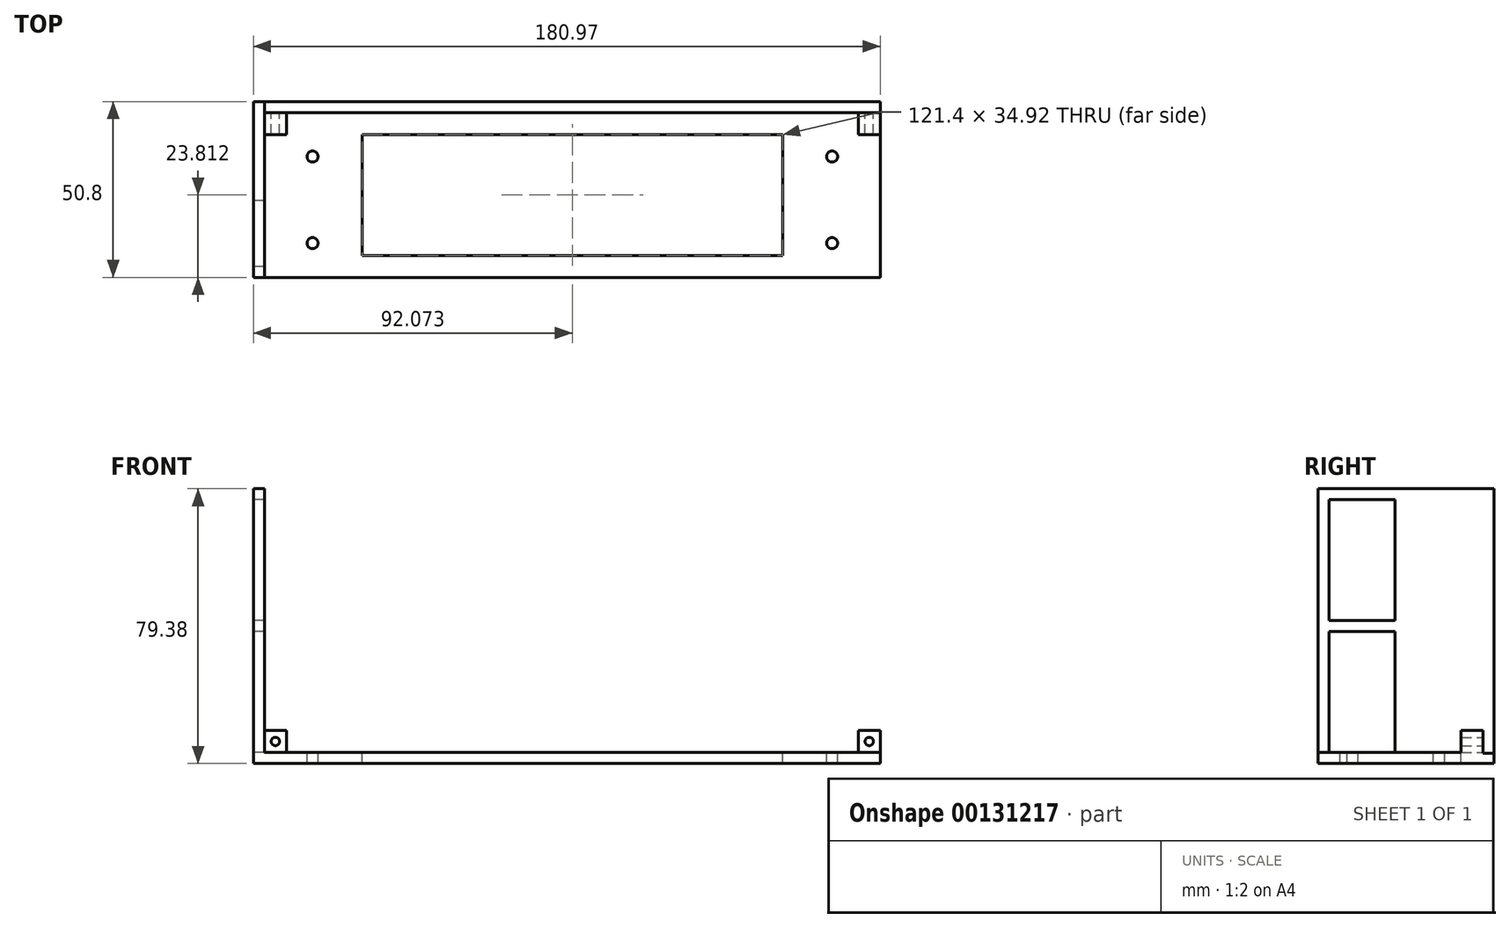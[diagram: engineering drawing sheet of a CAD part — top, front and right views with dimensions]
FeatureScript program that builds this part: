
annotation { "Feature Type Name" : "Feature", "Feature Type Description" : "" }
export const myFeature = defineFeature(function(context is Context, id is Id, definition is map)
    precondition{}
    {
        {
            var Q0;
            Q0=qCreatedBy(makeId("Top.planeOp"),FACE);
            var sketch = newSketch(context, id + "F0", { "sketchPlane" : qUnion([Q0])});
            skLineSegment(sketch, "E0.bottom", {"start": v(-95.97, 25.4) * mm, "end": v(88.18, 25.4) * mm});
            skLineSegment(sketch, "E0.top", {"start": v(-95.97, -25.4) * mm, "end": v(88.18, -25.4) * mm});
            skLineSegment(sketch, "E0.left", {"start": v(-95.97, 25.4) * mm, "end": v(-95.97, -25.4) * mm});
            skLineSegment(sketch, "E0.right", {"start": v(88.18, 25.4) * mm, "end": v(88.18, -25.4) * mm});
            skPoint(sketch, "E0.middle", {"position": v(-3.9, 0) * mm});
            skSolve(sketch);
        }
        {
            var Q0;
            Q0=makeQuery(id+"F0.imprint","IMPRINT",FACE,{"disambiguationData":[TD([[makeQuery(id+"F0.imprint","IMPRINT",EDGE,{"derivedFrom":sQuery(id+"F0.wireOp",EDGE,"E0.bottom")}),-1.0]])]});
            extrude(context, id + "F1", {"entities" : qUnion([Q0]), "depth" : 3.17 * mm});
        }
        {
            var Q0;
            Q0=makeQuery(id+"F1.opExtrude","CAP_FACE",FACE,{"disambiguationData":[OSD([sQuery(id+"F0.wireOp",EDGE,"E0.bottom"),sQuery(id+"F0.wireOp",EDGE,"E0.top"),sQuery(id+"F0.wireOp",EDGE,"E0.left"),sQuery(id+"F0.wireOp",EDGE,"E0.right")])],"isStart":false});
            var sketch = newSketch(context, id + "F2", { "sketchPlane" : qUnion([Q0])});
            skPoint(sketch, "E1", {"position": v(-78.9, 9.53) * mm});
            skPoint(sketch, "E2", {"position": v(71.1, 9.53) * mm});
            skPoint(sketch, "E3", {"position": v(71.1, -15.47) * mm});
            skPoint(sketch, "E4", {"position": v(-78.9, -15.47) * mm});
            skLineSegment(sketch, "E5", {"start": v(-78.9, 9.53) * mm, "end": v(-95.97, 9.53) * mm, "construction": true});
            skLineSegment(sketch, "E6", {"start": v(71.1, 9.53) * mm, "end": v(88.18, 9.53) * mm, "construction": true});
            skPoint(sketch, "E6.endSnap0", {"position": v(88.18, 0) * mm});
            skSolve(sketch);
        }
        {
            var Q0;
            Q0=sQuery(id+"F2.wireOp",VERTEX,"E1");
            var Q1;
            Q1=sQuery(id+"F2.wireOp",VERTEX,"E4");
            var Q2;
            Q2=sQuery(id+"F2.wireOp",VERTEX,"E3");
            var Q3;
            Q3=sQuery(id+"F2.wireOp",VERTEX,"E2");
            var Q4;
            Q4=makeQuery(id+"F1.opExtrude","SWEPT_BODY",BODY,{"disambiguationData":[OSD([sQuery(id+"F0.wireOp",EDGE,"E0.bottom"),sQuery(id+"F0.wireOp",EDGE,"E0.top"),sQuery(id+"F0.wireOp",EDGE,"E0.left"),sQuery(id+"F0.wireOp",EDGE,"E0.right")])]});
            hole(context, id + "F3", {"style" : HoleStyle.SIMPLE, "endStyle" : HoleEndStyle.THROUGH, "standardTappedOrClearance" : lookupTablePath({ "standard" : "ISO", "engagement" : "75%", "pitch" : "0.75 mm", "size" : "M4", "type" : "Tapped" }), "standardBlindInLast" : lookupTablePath({ "standard" : "ISO", "engagement" : "75%", "pitch" : "0.75 mm", "size" : "M4", "type" : "Tapped" }), "holeDiameter" : 3.2 * mm, "locations" : qUnion([Q0, Q1, Q2, Q3]), "scope" : qUnion([Q4]), "isTappedThrough" : true, "showTappedDepth" : true});
        }
        {
            var Q0;
            Q0=makeQuery(id+"F1.opExtrude","CAP_FACE",FACE,{"disambiguationData":[OSD([sQuery(id+"F0.wireOp",EDGE,"E0.bottom"),sQuery(id+"F0.wireOp",EDGE,"E0.top"),sQuery(id+"F0.wireOp",EDGE,"E0.left"),sQuery(id+"F0.wireOp",EDGE,"E0.right")])],"isStart":false});
            var sketch = newSketch(context, id + "F4", { "sketchPlane" : qUnion([Q0])});
            skLineSegment(sketch, "E7.bottom", {"start": v(-95.97, 25.4) * mm, "end": v(88.18, 25.4) * mm});
            skLineSegment(sketch, "E7.top", {"start": v(-95.97, 22.23) * mm, "end": v(88.18, 22.23) * mm});
            skLineSegment(sketch, "E7.left", {"start": v(-95.97, 25.4) * mm, "end": v(-95.97, 22.23) * mm});
            skLineSegment(sketch, "E7.right", {"start": v(88.18, 25.4) * mm, "end": v(88.18, 22.23) * mm});
            skSolve(sketch);
        }
        {
            var Q0;
            Q0=makeQuery(id+"F4.imprint","IMPRINT",FACE,{"disambiguationData":[TD([[makeQuery(id+"F4.imprint","IMPRINT",EDGE,{"derivedFrom":sQuery(id+"F4.wireOp",EDGE,"E7.bottom")}),-1.0]])]});
            extrude(context, id + "F5", {"entities" : qUnion([Q0]), "operationType" : NewBodyOperationType.ADD, "depth" : 76.2 * mm});
        }
        {
            var Q0;
            Q0=makeQuery(id+"F5.opExtrude","SWEPT_FACE",FACE,{"disambiguationData":[OSD([sQuery(id+"F4.wireOp",EDGE,"E7.top")])]});
            var sketch = newSketch(context, id + "F6", { "sketchPlane" : qUnion([Q0])});
            skPoint(sketch, "E8", {"position": v(-70.57, 66.67) * mm});
            skPoint(sketch, "E9", {"position": v(11.98, 66.67) * mm});
            skPoint(sketch, "E10", {"position": v(-64.22, 18.41) * mm});
            skPoint(sketch, "E11", {"position": v(10.7, 18.42) * mm});
            skSolve(sketch);
        }
        {
            var Q0;
            Q0=sQuery(id+"F6.wireOp",VERTEX,"E8");
            var Q1;
            Q1=sQuery(id+"F6.wireOp",VERTEX,"E9");
            var Q2;
            Q2=sQuery(id+"F6.wireOp",VERTEX,"E11");
            var Q3;
            Q3=sQuery(id+"F6.wireOp",VERTEX,"E10");
            var Q4;
            Q4=makeQuery(id+"F1.opExtrude","SWEPT_BODY",BODY,{"disambiguationData":[OSD([sQuery(id+"F0.wireOp",EDGE,"E0.bottom"),sQuery(id+"F0.wireOp",EDGE,"E0.top"),sQuery(id+"F0.wireOp",EDGE,"E0.left"),sQuery(id+"F0.wireOp",EDGE,"E0.right")])]});
            hole(context, id + "F7", {"style" : HoleStyle.SIMPLE, "endStyle" : HoleEndStyle.THROUGH, "standardTappedOrClearance" : lookupTablePath({ "standard" : "ISO", "fit" : "Normal", "size" : "M3", "type" : "Clearance" }), "standardBlindInLast" : lookupTablePath({ "fit" : "Standard", "standard" : "ISO", "size" : "M3", "type" : "Clearance" }), "holeDiameter" : 3.3 * mm, "locations" : qUnion([Q0, Q1, Q2, Q3]), "scope" : qUnion([Q4]), "isTappedThrough" : true});
        }
        {
            var Q0;
            Q0=makeQuery(id+"F1.opExtrude","CAP_FACE",FACE,{"disambiguationData":[OSD([sQuery(id+"F0.wireOp",EDGE,"E0.bottom"),sQuery(id+"F0.wireOp",EDGE,"E0.top"),sQuery(id+"F0.wireOp",EDGE,"E0.left"),sQuery(id+"F0.wireOp",EDGE,"E0.right")])],"isStart":false});
            var sketch = newSketch(context, id + "F8", { "sketchPlane" : qUnion([Q0])});
            skLineSegment(sketch, "E12.bottom", {"start": v(-95.97, 22.23) * mm, "end": v(-92.8, 22.23) * mm});
            skLineSegment(sketch, "E12.top", {"start": v(-95.97, -25.4) * mm, "end": v(-92.8, -25.4) * mm});
            skLineSegment(sketch, "E12.left", {"start": v(-95.97, 22.23) * mm, "end": v(-95.97, -25.4) * mm});
            skLineSegment(sketch, "E12.right", {"start": v(-92.8, 22.23) * mm, "end": v(-92.8, -25.4) * mm});
            skSolve(sketch);
        }
        {
            var Q0;
            Q0=makeQuery(id+"F8.imprint","IMPRINT",FACE,{"disambiguationData":[TD([[makeQuery(id+"F8.imprint","IMPRINT",EDGE,{"derivedFrom":sQuery(id+"F8.wireOp",EDGE,"E12.bottom")}),-1.0]])]});
            extrude(context, id + "F9", {"entities" : qUnion([Q0]), "operationType" : NewBodyOperationType.ADD, "depth" : 76.2 * mm});
        }
        {
            var Q0;
            Q0=makeQuery(id+"F9.boolean.opBoolean","MERGE",FACE,{"derivedFrom":[makeQuery(id+"F5.boolean.opBoolean","MERGE",FACE,{"derivedFrom":[makeQuery(id+"F1.opExtrude","SWEPT_FACE",FACE,{"disambiguationData":[OSD([sQuery(id+"F0.wireOp",EDGE,"E0.left")])]}),makeQuery(id+"F5.opExtrude","SWEPT_FACE",FACE,{"disambiguationData":[OSD([sQuery(id+"F4.wireOp",EDGE,"E7.left")])]})]}),makeQuery(id+"F9.opExtrude","SWEPT_FACE",FACE,{"disambiguationData":[OSD([sQuery(id+"F8.wireOp",EDGE,"E12.left")])]})]});
            var sketch = newSketch(context, id + "F10", { "sketchPlane" : qUnion([Q0])});
            skLineSegment(sketch, "E13.bottom", {"start": v(3.18, 76.2) * mm, "end": v(22.23, 76.2) * mm});
            skLineSegment(sketch, "E13.top", {"start": v(3.18, 3.18) * mm, "end": v(22.23, 3.18) * mm});
            skLineSegment(sketch, "E13.left", {"start": v(3.18, 76.2) * mm, "end": v(3.18, 3.17) * mm});
            skLineSegment(sketch, "E13.right", {"start": v(22.23, 76.2) * mm, "end": v(22.23, 3.17) * mm});
            skLineSegment(sketch, "E14", {"start": v(3.18, 39.69) * mm, "end": v(22.23, 39.69) * mm});
            skLineSegment(sketch, "E15", {"start": v(3.18, 41.27) * mm, "end": v(22.23, 41.27) * mm});
            skLineSegment(sketch, "E16", {"start": v(3.18, 38.1) * mm, "end": v(22.23, 38.1) * mm});
            skSolve(sketch);
        }
        {
            var Q0;
            {var subQ0=sQuery(id+"F10.wireOp",EDGE,"E13.bottom");Q0=makeQuery(id+"F10.imprint","IMPRINT",FACE,{"disambiguationData":[TD([[makeQuery(id+"F10.imprint","IMPRINT",EDGE,{"derivedFrom":subQ0}),-1.0]])]});}
            var Q1;
            {var subQ0=sQuery(id+"F10.wireOp",EDGE,"E13.top");Q1=makeQuery(id+"F10.imprint","IMPRINT",FACE,{"disambiguationData":[TD([[makeQuery(id+"F10.imprint","IMPRINT",EDGE,{"derivedFrom":subQ0}),1.0]])]});}
            extrude(context, id + "F11", {"entities" : qUnion([Q0, Q1]), "operationType" : NewBodyOperationType.REMOVE, "endBound" : BoundingType.UP_TO_NEXT, "oppositeDirection" : true, "depth" : 25.4 * mm});
        }
        {
            var Q0;
            Q0=makeQuery(id+"F11.boolean.opBoolean","MERGE",FACE,{"derivedFrom":[makeQuery(id+"F1.opExtrude","CAP_FACE",FACE,{"disambiguationData":[OSD([sQuery(id+"F0.wireOp",EDGE,"E0.bottom"),sQuery(id+"F0.wireOp",EDGE,"E0.top"),sQuery(id+"F0.wireOp",EDGE,"E0.left"),sQuery(id+"F0.wireOp",EDGE,"E0.right")])],"isStart":false}),makeQuery(id+"F11.opExtrude","SWEPT_FACE",FACE,{"disambiguationData":[OSD([sQuery(id+"F10.wireOp",EDGE,"E13.top")])]})]});
            var sketch = newSketch(context, id + "F12", { "sketchPlane" : qUnion([Q0])});
            skLineSegment(sketch, "E17.bottom", {"start": v(88.18, 22.23) * mm, "end": v(85, 22.23) * mm});
            skLineSegment(sketch, "E17.top", {"start": v(88.18, -25.4) * mm, "end": v(85, -25.4) * mm});
            skLineSegment(sketch, "E17.left", {"start": v(88.18, 22.23) * mm, "end": v(88.18, -25.4) * mm});
            skLineSegment(sketch, "E17.right", {"start": v(85, 22.23) * mm, "end": v(85, -25.4) * mm});
            skSolve(sketch);
        }
        {
            var Q0;
            Q0=makeQuery(id+"F12.imprint","IMPRINT",FACE,{"disambiguationData":[TD([[makeQuery(id+"F12.imprint","IMPRINT",EDGE,{"derivedFrom":sQuery(id+"F12.wireOp",EDGE,"E17.bottom")}),-1.0]])]});
            extrude(context, id + "F13", {"entities" : qUnion([Q0]), "operationType" : NewBodyOperationType.ADD, "depth" : 76.2 * mm});
        }
        {
            var Q0;
            Q0=makeQuery(id+"F13.boolean.opBoolean","MERGE",FACE,{"derivedFrom":[makeQuery(id+"F5.boolean.opBoolean","MERGE",FACE,{"derivedFrom":[makeQuery(id+"F1.opExtrude","SWEPT_FACE",FACE,{"disambiguationData":[OSD([sQuery(id+"F0.wireOp",EDGE,"E0.right")])]}),makeQuery(id+"F5.opExtrude","SWEPT_FACE",FACE,{"disambiguationData":[OSD([sQuery(id+"F4.wireOp",EDGE,"E7.right")])]})]}),makeQuery(id+"F13.opExtrude","SWEPT_FACE",FACE,{"disambiguationData":[OSD([sQuery(id+"F12.wireOp",EDGE,"E17.left")])]})]});
            var sketch = newSketch(context, id + "F14", { "sketchPlane" : qUnion([Q0])});
            skLineSegment(sketch, "E18.bottom", {"start": v(-22.22, 3.17) * mm, "end": v(22.23, 3.18) * mm});
            skLineSegment(sketch, "E18.top", {"start": v(-22.22, 34.92) * mm, "end": v(22.23, 34.93) * mm});
            skLineSegment(sketch, "E18.left", {"start": v(-22.22, 3.17) * mm, "end": v(-22.22, 34.92) * mm});
            skLineSegment(sketch, "E18.right", {"start": v(22.23, 3.17) * mm, "end": v(22.23, 34.92) * mm});
            skLineSegment(sketch, "E19", {"start": v(-7.4, 34.92) * mm, "end": v(-7.4, 3.18) * mm, "construction": true});
            skLineSegment(sketch, "E20", {"start": v(7.4, 34.92) * mm, "end": v(7.4, 3.18) * mm, "construction": true});
            skLineSegment(sketch, "E21", {"start": v(-22.22, 19.05) * mm, "end": v(-7.4, 19.05) * mm, "construction": true});
            skLineSegment(sketch, "E22", {"start": v(-7.4, 19.05) * mm, "end": v(7.4, 19.05) * mm, "construction": true});
            skLineSegment(sketch, "E23", {"start": v(7.4, 19.05) * mm, "end": v(22.23, 19.05) * mm, "construction": true});
            skLineSegment(sketch, "E24.bottom", {"start": v(-9, 34.92) * mm, "end": v(-5.82, 34.92) * mm});
            skLineSegment(sketch, "E24.top", {"start": v(-9, 3.17) * mm, "end": v(-5.82, 3.17) * mm});
            skLineSegment(sketch, "E24.left", {"start": v(-9, 34.92) * mm, "end": v(-9, 3.17) * mm});
            skLineSegment(sketch, "E24.right", {"start": v(-5.82, 34.92) * mm, "end": v(-5.82, 3.17) * mm});
            skPoint(sketch, "E24.middle", {"position": v(-7.4, 19.05) * mm});
            skLineSegment(sketch, "E25.bottom", {"start": v(5.82, 34.92) * mm, "end": v(9, 34.92) * mm});
            skLineSegment(sketch, "E25.top", {"start": v(5.82, 3.17) * mm, "end": v(9, 3.17) * mm});
            skLineSegment(sketch, "E25.left", {"start": v(5.82, 34.92) * mm, "end": v(5.82, 3.17) * mm});
            skLineSegment(sketch, "E25.right", {"start": v(9, 34.92) * mm, "end": v(9, 3.17) * mm});
            skPoint(sketch, "E25.middle", {"position": v(7.4, 19.05) * mm});
            skSolve(sketch);
        }
        {
            var Q0;
            {var subQ0=sQuery(id+"F14.wireOp",EDGE,"E18.left");Q0=makeQuery(id+"F14.imprint","IMPRINT",FACE,{"disambiguationData":[TD([[makeQuery(id+"F14.imprint","IMPRINT",EDGE,{"derivedFrom":subQ0}),-1.0]])]});}
            var Q1;
            {var subQ0=sQuery(id+"F14.wireOp",EDGE,"E24.right");Q1=makeQuery(id+"F14.imprint","IMPRINT",FACE,{"disambiguationData":[TD([[makeQuery(id+"F14.imprint","IMPRINT",EDGE,{"derivedFrom":subQ0}),1.0]])]});}
            var Q2;
            {var subQ0=sQuery(id+"F14.wireOp",EDGE,"E18.right");Q2=makeQuery(id+"F14.imprint","IMPRINT",FACE,{"disambiguationData":[TD([[makeQuery(id+"F14.imprint","IMPRINT",EDGE,{"derivedFrom":subQ0}),1.0]])]});}
            extrude(context, id + "F15", {"entities" : qUnion([Q0, Q1, Q2]), "operationType" : NewBodyOperationType.REMOVE, "endBound" : BoundingType.UP_TO_NEXT, "oppositeDirection" : true, "depth" : 25.4 * mm});
        }
        {
            var Q0;
            Q0=makeQuery(id+"F15.boolean.opBoolean","MERGE",FACE,{"derivedFrom":[makeQuery(id+"F5.opExtrude","SWEPT_FACE",FACE,{"disambiguationData":[OSD([sQuery(id+"F4.wireOp",EDGE,"E7.top")])]}),makeQuery(id+"F15.opExtrude","SWEPT_FACE",FACE,{"disambiguationData":[OSD([sQuery(id+"F14.wireOp",EDGE,"E18.right")])]})]});
            var sketch = newSketch(context, id + "F16", { "sketchPlane" : qUnion([Q0])});
            skLineSegment(sketch, "E26.bottom", {"start": v(-92.8, 79.38) * mm, "end": v(-86.45, 79.38) * mm});
            skLineSegment(sketch, "E26.top", {"start": v(-92.8, 73.03) * mm, "end": v(-86.45, 73.03) * mm});
            skLineSegment(sketch, "E26.left", {"start": v(-92.8, 79.38) * mm, "end": v(-92.8, 73.03) * mm});
            skLineSegment(sketch, "E26.right", {"start": v(-86.45, 79.38) * mm, "end": v(-86.45, 73.03) * mm});
            skLineSegment(sketch, "E27.bottom", {"start": v(85, 79.38) * mm, "end": v(78.65, 79.38) * mm});
            skLineSegment(sketch, "E27.top", {"start": v(85, 73.03) * mm, "end": v(78.65, 73.03) * mm});
            skLineSegment(sketch, "E27.left", {"start": v(85, 79.38) * mm, "end": v(85, 73.03) * mm});
            skLineSegment(sketch, "E27.right", {"start": v(78.65, 79.38) * mm, "end": v(78.65, 73.03) * mm});
            skSolve(sketch);
        }
        {
            var Q0;
            Q0=makeQuery(id+"F16.imprint","IMPRINT",FACE,{"disambiguationData":[TD([[makeQuery(id+"F16.imprint","IMPRINT",EDGE,{"derivedFrom":sQuery(id+"F16.wireOp",EDGE,"E26.bottom")}),-1.0]])]});
            var Q1;
            Q1=makeQuery(id+"F16.imprint","IMPRINT",FACE,{"disambiguationData":[TD([[makeQuery(id+"F16.imprint","IMPRINT",EDGE,{"derivedFrom":sQuery(id+"F16.wireOp",EDGE,"E26.bottom")}),-1.0]])]});
            var Q2;
            Q2=makeQuery(id+"F16.imprint","IMPRINT",FACE,{"disambiguationData":[TD([[makeQuery(id+"F16.imprint","IMPRINT",EDGE,{"derivedFrom":sQuery(id+"F16.wireOp",EDGE,"E27.bottom")}),-1.0]])]});
            extrude(context, id + "F17", {"entities" : qUnion([Q0, Q1, Q2]), "operationType" : NewBodyOperationType.ADD, "depth" : 6.35 * mm});
        }
        {
            var Q0;
            Q0=makeQuery(id+"F17.boolean.opBoolean","MERGE",FACE,{"derivedFrom":[makeQuery(id+"F13.boolean.opBoolean","MERGE",FACE,{"derivedFrom":[makeQuery(id+"F9.boolean.opBoolean","MERGE",FACE,{"derivedFrom":[makeQuery(id+"F5.opExtrude","CAP_FACE",FACE,{"disambiguationData":[OSD([sQuery(id+"F4.wireOp",EDGE,"E7.bottom"),sQuery(id+"F4.wireOp",EDGE,"E7.top"),sQuery(id+"F4.wireOp",EDGE,"E7.left"),sQuery(id+"F4.wireOp",EDGE,"E7.right")])],"isStart":false}),makeQuery(id+"F9.opExtrude","CAP_FACE",FACE,{"disambiguationData":[OSD([sQuery(id+"F8.wireOp",EDGE,"E12.bottom"),sQuery(id+"F8.wireOp",EDGE,"E12.top"),sQuery(id+"F8.wireOp",EDGE,"E12.left"),sQuery(id+"F8.wireOp",EDGE,"E12.right")])],"isStart":false})]}),makeQuery(id+"F13.opExtrude","CAP_FACE",FACE,{"disambiguationData":[OSD([sQuery(id+"F12.wireOp",EDGE,"E17.bottom"),sQuery(id+"F12.wireOp",EDGE,"E17.top"),sQuery(id+"F12.wireOp",EDGE,"E17.left"),sQuery(id+"F12.wireOp",EDGE,"E17.right")])],"isStart":false})]}),makeQuery(id+"F17.opExtrude","SWEPT_FACE",FACE,{"disambiguationData":[OSD([sQuery(id+"F16.wireOp",EDGE,"E26.bottom")])]}),makeQuery(id+"F17.opExtrude","SWEPT_FACE",FACE,{"disambiguationData":[OSD([sQuery(id+"F16.wireOp",EDGE,"E27.bottom")])]})]});
            var sketch = newSketch(context, id + "F18", { "sketchPlane" : qUnion([Q0])});
            skPoint(sketch, "E28", {"position": v(-89.62, 19.05) * mm});
            skPoint(sketch, "E29", {"position": v(81.83, 19.05) * mm});
            skSolve(sketch);
        }
        {
            var Q0;
            Q0=sQuery(id+"F18.wireOp",VERTEX,"E28");
            var Q1;
            Q1=sQuery(id+"F18.wireOp",VERTEX,"E29");
            var Q2;
            Q2=makeQuery(id+"F1.opExtrude","SWEPT_BODY",BODY,{"disambiguationData":[OSD([sQuery(id+"F0.wireOp",EDGE,"E0.bottom"),sQuery(id+"F0.wireOp",EDGE,"E0.top"),sQuery(id+"F0.wireOp",EDGE,"E0.left"),sQuery(id+"F0.wireOp",EDGE,"E0.right")])]});
            hole(context, id + "F19", {"style" : HoleStyle.SIMPLE, "endStyle" : HoleEndStyle.BLIND, "standardTappedOrClearance" : lookupTablePath({ "standard" : "ISO", "engagement" : "75%", "pitch" : "0.6 mm", "size" : "M3", "type" : "Tapped" }), "standardBlindInLast" : lookupTablePath({ "standard" : "ISO", "engagement" : "75%", "pitch" : "0.6 mm", "size" : "M3", "type" : "Tapped" }), "holeDiameter" : 2.4 * mm, "holeDepth" : 12.7 * mm, "locations" : qUnion([Q0, Q1]), "scope" : qUnion([Q2])});
        }
        {
            var Q0;
            {var subQ0=sQuery(id+"F14.wireOp",EDGE,"E18.bottom");var subQ2=sQuery(id+"F14.wireOp",EDGE,"E24.top");Q0=makeQuery(id+"F15.boolean.opBoolean","MERGE",FACE,{"derivedFrom":[makeQuery(id+"F11.boolean.opBoolean","MERGE",FACE,{"derivedFrom":[makeQuery(id+"F1.opExtrude","CAP_FACE",FACE,{"disambiguationData":[OSD([sQuery(id+"F0.wireOp",EDGE,"E0.bottom"),sQuery(id+"F0.wireOp",EDGE,"E0.top"),sQuery(id+"F0.wireOp",EDGE,"E0.left"),sQuery(id+"F0.wireOp",EDGE,"E0.right")])],"isStart":false}),makeQuery(id+"F11.opExtrude","SWEPT_FACE",FACE,{"disambiguationData":[OSD([sQuery(id+"F10.wireOp",EDGE,"E13.top")])]})]}),makeQuery(id+"F15.opExtrude","SWEPT_FACE",FACE,{"disambiguationData":[OSD([subQ0]),TDD([makeQuery(id+"F14.imprint","IMPRINT",EDGE,{"disambiguationData":[TD([[makeQuery(id+"F14.imprint","INTERSECT",VERTEX,{"derivedFrom":[subQ0,sQuery(id+"F14.wireOp",EDGE,"E18.left")]}),-1.0]])],"derivedFrom":subQ0})])]}),makeQuery(id+"F15.opExtrude","SWEPT_FACE",FACE,{"disambiguationData":[OSD([subQ0]),TDD([makeQuery(id+"F14.imprint","IMPRINT",EDGE,{"disambiguationData":[TD([[makeQuery(id+"F14.imprint","INTERSECT",VERTEX,{"derivedFrom":[subQ0,subQ2,sQuery(id+"F14.wireOp",EDGE,"E24.right")]}),-1.0]])],"derivedFrom":subQ0})])]}),makeQuery(id+"F15.opExtrude","SWEPT_FACE",FACE,{"disambiguationData":[OSD([subQ0]),TDD([makeQuery(id+"F14.imprint","IMPRINT",EDGE,{"disambiguationData":[TD([[makeQuery(id+"F14.imprint","INTERSECT",VERTEX,{"derivedFrom":[subQ0,sQuery(id+"F14.wireOp",EDGE,"E18.right")]}),1.0]])],"derivedFrom":subQ0})])]})]});}
            var sketch = newSketch(context, id + "F20", { "sketchPlane" : qUnion([Q0])});
            skLineSegment(sketch, "E30.bottom", {"start": v(-64.6, -19.05) * mm, "end": v(56.8, -19.05) * mm});
            skLineSegment(sketch, "E30.top", {"start": v(-64.6, 15.88) * mm, "end": v(56.8, 15.88) * mm});
            skLineSegment(sketch, "E30.left", {"start": v(-64.6, -19.05) * mm, "end": v(-64.6, 15.88) * mm});
            skLineSegment(sketch, "E30.right", {"start": v(56.8, -19.05) * mm, "end": v(56.8, 15.88) * mm});
            skSolve(sketch);
        }
        {
            var Q0;
            Q0=makeQuery(id+"F20.imprint","IMPRINT",FACE,{"disambiguationData":[TD([[makeQuery(id+"F20.imprint","IMPRINT",EDGE,{"derivedFrom":sQuery(id+"F20.wireOp",EDGE,"E30.bottom")}),1.0]])]});
            extrude(context, id + "F21", {"entities" : qUnion([Q0]), "operationType" : NewBodyOperationType.REMOVE, "oppositeDirection" : true, "depth" : 25.4 * mm});
        }
        {
            var Q0;
            Q0=makeQuery(id+"F15.boolean.opBoolean","MERGE",FACE,{"derivedFrom":[makeQuery(id+"F5.opExtrude","SWEPT_FACE",FACE,{"disambiguationData":[OSD([sQuery(id+"F4.wireOp",EDGE,"E7.top")])]}),makeQuery(id+"F15.opExtrude","SWEPT_FACE",FACE,{"disambiguationData":[OSD([sQuery(id+"F14.wireOp",EDGE,"E18.right")])]})]});
            var sketch = newSketch(context, id + "F22", { "sketchPlane" : qUnion([Q0])});
            skLineSegment(sketch, "E31.bottom", {"start": v(-56.22, 58.67) * mm, "end": v(3.98, 58.67) * mm});
            skLineSegment(sketch, "E31.top", {"start": v(-56.22, 26.42) * mm, "end": v(3.98, 26.42) * mm});
            skLineSegment(sketch, "E31.left", {"start": v(-56.22, 58.67) * mm, "end": v(-56.22, 26.42) * mm});
            skLineSegment(sketch, "E31.right", {"start": v(3.98, 58.67) * mm, "end": v(3.98, 26.42) * mm});
            skSolve(sketch);
        }
        {
            var Q0;
            Q0=makeQuery(id+"F22.imprint","IMPRINT",FACE,{"disambiguationData":[TD([[makeQuery(id+"F22.imprint","IMPRINT",EDGE,{"derivedFrom":sQuery(id+"F22.wireOp",EDGE,"E31.bottom")}),-1.0]])]});
            extrude(context, id + "F23", {"entities" : qUnion([Q0]), "operationType" : NewBodyOperationType.REMOVE, "oppositeDirection" : true, "depth" : 25.4 * mm});
        }
        {
            var Q0;
            Q0=makeQuery(id+"F13.boolean.opBoolean","MERGE",FACE,{"derivedFrom":[makeQuery(id+"F9.boolean.opBoolean","MERGE",FACE,{"derivedFrom":[makeQuery(id+"F1.opExtrude","SWEPT_FACE",FACE,{"disambiguationData":[OSD([sQuery(id+"F0.wireOp",EDGE,"E0.top")])]}),makeQuery(id+"F9.opExtrude","SWEPT_FACE",FACE,{"disambiguationData":[OSD([sQuery(id+"F8.wireOp",EDGE,"E12.top")])]})]}),makeQuery(id+"F13.opExtrude","SWEPT_FACE",FACE,{"disambiguationData":[OSD([sQuery(id+"F12.wireOp",EDGE,"E17.top")])]})]});
            var sketch = newSketch(context, id + "F24", { "sketchPlane" : qUnion([Q0])});
            skLineSegment(sketch, "E32", {"start": v(-92.8, 79.38) * mm, "end": v(-92.8, 3.17) * mm});
            skLineSegment(sketch, "E33", {"start": v(-92.8, 3.17) * mm, "end": v(85, 3.18) * mm});
            skLineSegment(sketch, "E34", {"start": v(85, 3.18) * mm, "end": v(85, 0) * mm});
            skLineSegment(sketch, "E35", {"start": v(85, 0) * mm, "end": v(88.18, 0) * mm});
            skLineSegment(sketch, "E36", {"start": v(88.18, 0) * mm, "end": v(88.18, 79.38) * mm});
            skLineSegment(sketch, "E37", {"start": v(88.18, 79.38) * mm, "end": v(-92.8, 79.38) * mm});
            skSolve(sketch);
        }
        {
            var Q0;
            {var subQ0=sQuery(id+"F24.wireOp",EDGE,"E32");Q0=makeQuery(id+"F24.imprint","IMPRINT",FACE,{"disambiguationData":[TD([[makeQuery(id+"F24.imprint","IMPRINT",EDGE,{"derivedFrom":subQ0}),1.0]])]});}
            var Q1;
            Q1=makeQuery(id+"F24.imprint","IMPRINT",FACE,{"disambiguationData":[TD([[makeQuery(id+"F24.imprint","IMPRINT",EDGE,{"derivedFrom":sQuery(id+"F24.wireOp",EDGE,"E34")}),1.0]])]});
            extrude(context, id + "F25", {"entities" : qUnion([Q0, Q1]), "operationType" : NewBodyOperationType.REMOVE, "endBound" : BoundingType.THROUGH_ALL, "oppositeDirection" : true, "depth" : 25.4 * mm});
        }
        {
            var Q0;
            Q0=makeQuery(id+"F5.boolean.opBoolean","MERGE",FACE,{"derivedFrom":[makeQuery(id+"F1.opExtrude","SWEPT_FACE",FACE,{"disambiguationData":[OSD([sQuery(id+"F0.wireOp",EDGE,"E0.bottom")])]}),makeQuery(id+"F5.opExtrude","SWEPT_FACE",FACE,{"disambiguationData":[OSD([sQuery(id+"F4.wireOp",EDGE,"E7.bottom")])]})]});
            var sketch = newSketch(context, id + "F26", { "sketchPlane" : qUnion([Q0])});
            skLineSegment(sketch, "E38.bottom", {"start": v(-85, 3.18) * mm, "end": v(-78.65, 3.18) * mm});
            skLineSegment(sketch, "E38.top", {"start": v(-85, 9.53) * mm, "end": v(-78.65, 9.53) * mm});
            skLineSegment(sketch, "E38.left", {"start": v(-85, 3.18) * mm, "end": v(-85, 9.53) * mm});
            skLineSegment(sketch, "E38.right", {"start": v(-78.65, 3.18) * mm, "end": v(-78.65, 9.53) * mm});
            skLineSegment(sketch, "E39.bottom", {"start": v(92.8, 3.18) * mm, "end": v(86.45, 3.18) * mm});
            skLineSegment(sketch, "E39.top", {"start": v(92.8, 9.53) * mm, "end": v(86.45, 9.53) * mm});
            skLineSegment(sketch, "E39.left", {"start": v(92.8, 3.18) * mm, "end": v(92.8, 9.53) * mm});
            skLineSegment(sketch, "E39.right", {"start": v(86.45, 3.17) * mm, "end": v(86.45, 9.53) * mm});
            skPoint(sketch, "E40", {"position": v(-81.83, 6.35) * mm});
            skPoint(sketch, "E40.positionSnap0", {"position": v(-81.83, 9.53) * mm});
            skPoint(sketch, "E40.positionSnap1", {"position": v(-85, 6.35) * mm});
            skPoint(sketch, "E41", {"position": v(89.62, 6.35) * mm});
            skSolve(sketch);
        }
        {
            var Q0;
            Q0=makeQuery(id+"F26.imprint","IMPRINT",FACE,{"disambiguationData":[TD([[makeQuery(id+"F26.imprint","IMPRINT",EDGE,{"derivedFrom":sQuery(id+"F26.wireOp",EDGE,"E38.bottom")}),1.0]])]});
            var Q1;
            Q1=makeQuery(id+"F26.imprint","IMPRINT",FACE,{"disambiguationData":[TD([[makeQuery(id+"F26.imprint","IMPRINT",EDGE,{"derivedFrom":sQuery(id+"F26.wireOp",EDGE,"E39.bottom")}),1.0]])]});
            extrude(context, id + "F27", {"entities" : qUnion([Q0, Q1]), "operationType" : NewBodyOperationType.ADD, "oppositeDirection" : true, "depth" : 9.52 * mm});
        }
        {
            var Q0;
            Q0=sQuery(id+"F26.wireOp",VERTEX,"E41");
            var Q1;
            Q1=sQuery(id+"F26.wireOp",VERTEX,"E40");
            var Q2;
            Q2=makeQuery(id+"F1.opExtrude","SWEPT_BODY",BODY,{"disambiguationData":[OSD([sQuery(id+"F0.wireOp",EDGE,"E0.bottom"),sQuery(id+"F0.wireOp",EDGE,"E0.top"),sQuery(id+"F0.wireOp",EDGE,"E0.left"),sQuery(id+"F0.wireOp",EDGE,"E0.right")])]});
            hole(context, id + "F28", {"style" : HoleStyle.SIMPLE, "endStyle" : HoleEndStyle.BLIND, "standardTappedOrClearance" : lookupTablePath({ "standard" : "ISO", "engagement" : "75%", "pitch" : "0.6 mm", "size" : "M3", "type" : "Tapped" }), "standardBlindInLast" : lookupTablePath({ "standard" : "ISO", "engagement" : "75%", "pitch" : "0.6 mm", "size" : "M3", "type" : "Tapped" }), "holeDiameter" : 2.4 * mm, "holeDepth" : 12.7 * mm, "locations" : qUnion([Q0, Q1]), "scope" : qUnion([Q2])});
        }
        {
            var Q0;
            Q0=makeQuery(id+"F27.boolean.opBoolean","MERGE",FACE,{"derivedFrom":[makeQuery(id+"F5.boolean.opBoolean","MERGE",FACE,{"derivedFrom":[makeQuery(id+"F1.opExtrude","SWEPT_FACE",FACE,{"disambiguationData":[OSD([sQuery(id+"F0.wireOp",EDGE,"E0.bottom")])]}),makeQuery(id+"F5.opExtrude","SWEPT_FACE",FACE,{"disambiguationData":[OSD([sQuery(id+"F4.wireOp",EDGE,"E7.bottom")])]})]}),makeQuery(id+"F27.opExtrude","CAP_FACE",FACE,{"disambiguationData":[OSD([sQuery(id+"F26.wireOp",EDGE,"E38.bottom"),sQuery(id+"F26.wireOp",EDGE,"E38.top"),sQuery(id+"F26.wireOp",EDGE,"E38.left"),sQuery(id+"F26.wireOp",EDGE,"E38.right")])],"isStart":true}),makeQuery(id+"F27.opExtrude","CAP_FACE",FACE,{"disambiguationData":[OSD([sQuery(id+"F26.wireOp",EDGE,"E39.bottom"),sQuery(id+"F26.wireOp",EDGE,"E39.top"),sQuery(id+"F26.wireOp",EDGE,"E39.left"),sQuery(id+"F26.wireOp",EDGE,"E39.right")])],"isStart":true})]});
            var sketch = newSketch(context, id + "F29", { "sketchPlane" : qUnion([Q0])});
            skLineSegment(sketch, "E42.bottom", {"start": v(-85, 9.53) * mm, "end": v(92.8, 9.53) * mm});
            skLineSegment(sketch, "E42.top", {"start": v(-85, 2.93) * mm, "end": v(92.8, 2.93) * mm});
            skLineSegment(sketch, "E42.left", {"start": v(-85, 9.53) * mm, "end": v(-85, 2.93) * mm});
            skLineSegment(sketch, "E42.right", {"start": v(92.8, 9.53) * mm, "end": v(92.8, 2.93) * mm});
            skSolve(sketch);
        }
        {
            var Q0;
            {var subQ1=makeQuery(id+"F27.opExtrude","CAP_EDGE",EDGE,{"disambiguationData":[OSD([sQuery(id+"F26.wireOp",EDGE,"E38.right")])],"isStart":true});Q0=makeQuery(id+"F29.imprint","IMPRINT",FACE,{"disambiguationData":[TD([[makeQuery(id+"F29.imprint","IMPRINT",EDGE,{"derivedFrom":subQ1}),-1.0]])]});}
            var Q1;
            Q1=makeQuery(id+"F29.imprint","IMPRINT",FACE,{"disambiguationData":[TD([[makeQuery(id+"F29.imprint","IMPRINT",EDGE,{"derivedFrom":sQuery(id+"F29.wireOp",EDGE,"E42.top")}),1.0]])]});
            extrude(context, id + "F30", {"entities" : qUnion([Q0, Q1]), "operationType" : NewBodyOperationType.REMOVE, "oppositeDirection" : true, "depth" : 3.17 * mm});
        }
    });
